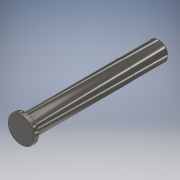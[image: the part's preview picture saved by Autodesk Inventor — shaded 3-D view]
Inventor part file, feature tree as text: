
AUTODESK INVENTOR PART (.ipt)
format: ipt  version: 2019 (Build 230136000, 136)  size: 126,976 bytes
history: native  units: mm
features: other x1, revolve x1, fillet x1, chamfer x1, sketch x1
ambient origin geometry x8: Origin, YZ Plane, XZ Plane, XY Plane, X Axis, Y Axis, Z Axis, Center Point
bodies: Body1 (feature_tree)
feature tree (5):
  other  "Твердое тело1"
  revolve  "Вращение1"
  fillet  "Сопряжение1"  Radius=64.0mm
  chamfer  "Фаска1"  Distance=9.3mm
  sketch  "Эскиз1"
